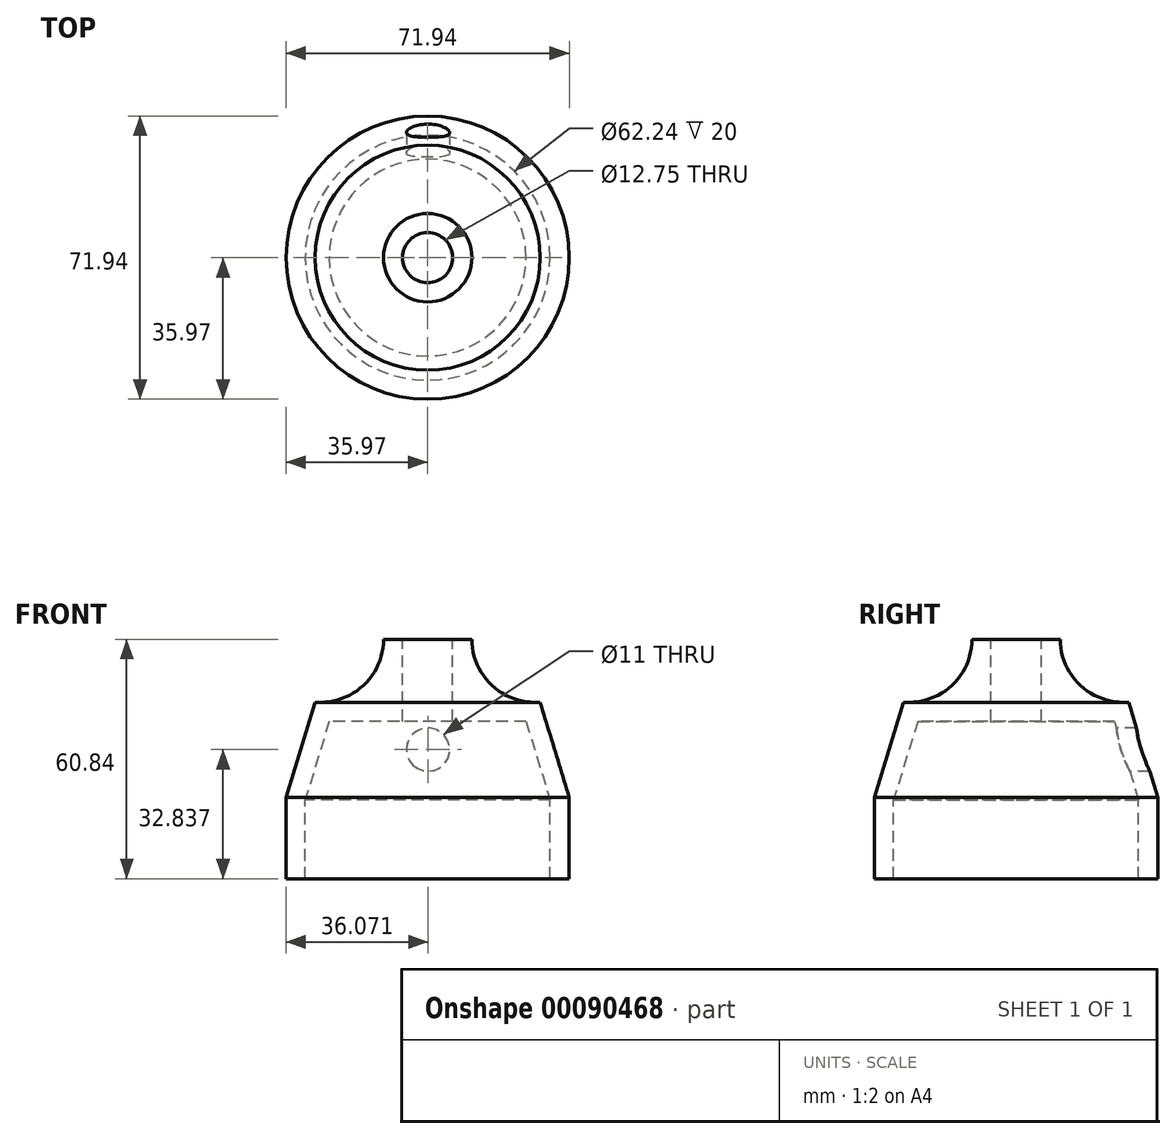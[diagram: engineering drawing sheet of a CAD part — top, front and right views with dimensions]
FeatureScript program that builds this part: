
annotation { "Feature Type Name" : "Feature", "Feature Type Description" : "" }
export const myFeature = defineFeature(function(context is Context, id is Id, definition is map)
    precondition{}
    {
        {
            var Q0;
            Q0=qCreatedBy(makeId("Front.planeOp"),FACE);
            var sketch = newSketch(context, id + "F0", { "sketchPlane" : qUnion([Q0])});
            skLineSegment(sketch, "E0.left", {"start": v(-31.12, -26.88) * mm, "end": v(-31.12, -6.88) * mm});
            skPoint(sketch, "E0.middle", {"position": v(0, -21.88) * mm});
            skLineSegment(sketch, "E1", {"start": v(-31.12, -6.88) * mm, "end": v(-25, 13.12) * mm});
            skLineSegment(sketch, "E2", {"start": v(0, 13.12) * mm, "end": v(0, -6.88) * mm});
            skPoint(sketch, "E3.middle", {"position": v(0, 13.12) * mm});
            skLineSegment(sketch, "E4", {"start": v(-25, 13.12) * mm, "end": v(-6.38, 13.12) * mm});
            skLineSegment(sketch, "E5.2", {"start": v(-35.97, -6.16) * mm, "end": v(-28.59, 17.96) * mm});
            skLineSegment(sketch, "E5.3", {"start": v(-35.97, -26.88) * mm, "end": v(-35.97, -6.16) * mm});
            skLineSegment(sketch, "E6", {"start": v(-35.97, -26.88) * mm, "end": v(-31.12, -26.88) * mm});
            skLineSegment(sketch, "E7", {"start": v(-28.59, 17.96) * mm, "end": v(-27.22, 17.96) * mm});
            skPoint(sketch, "E8.visualSharp", {"position": v(-11.22, 17.96) * mm});
            skArc(sketch, "E8.filletArc", {"start": v(-27.22, 17.96) * mm, "mid": v(-15.9, 22.65) * mm, "end": v(-11.22, 33.96) * mm});
            skLineSegment(sketch, "E9", {"start": v(-11.22, 33.96) * mm, "end": v(-6.38, 33.96) * mm});
            skLineSegment(sketch, "E10", {"start": v(-6.38, 33.96) * mm, "end": v(-6.38, 13.12) * mm});
            skSolve(sketch);
        }
        {
            var Q0;
            Q0=makeQuery(id+"F0.imprint","IMPRINT",FACE,{"disambiguationData":[TD([[makeQuery(id+"F0.imprint","IMPRINT",EDGE,{"derivedFrom":sQuery(id+"F0.wireOp",EDGE,"E0.left")}),1.0]])]});
            var Q1;
            Q1=sQuery(id+"F0.wireOp",EDGE,"E2");
            revolve(context, id + "F1", {"entities" : qUnion([Q0]), "axis" : qUnion([Q1]), "revolveType" : RevolveType.FULL});
        }
        {
            var Q0;
            Q0=qCreatedBy(makeId("Front.planeOp"),FACE);
            var sketch = newSketch(context, id + "F2", { "sketchPlane" : qUnion([Q0])});
            skLineSegment(sketch, "E11", {"start": v(-32.5, 5.96) * mm, "end": v(32.71, 5.96) * mm});
            skCircle(sketch, "E12", {"center": v(0.1, 5.96) * mm, "radius": 5.5 * mm});
            skSolve(sketch);
        }
        {
            var Q0;
            Q0 = qSketchRegion(id + "F2", true);
            extrude(context, id + "F3", {"entities" : qUnion([Q0]), "operationType" : NewBodyOperationType.REMOVE, "endBound" : BoundingType.THROUGH_ALL, "oppositeDirection" : true, "depth" : 25 * mm});
        }
        {
            var Q0;
            Q0=qCreatedBy(makeId("Front.planeOp"),FACE);
            var sketch = newSketch(context, id + "F4", { "sketchPlane" : qUnion([Q0])});
            skLineSegment(sketch, "E13", {"start": v(0, 0) * mm, "end": v(0, 45.74) * mm});
            skSolve(sketch);
        }
        {
            var Q0;
            Q0=makeQuery(id+"F1.opRevolve","SWEPT_BODY",BODY,{"disambiguationData":[OSD([sQuery(id+"F0.wireOp",EDGE,"E0.left"),sQuery(id+"F0.wireOp",EDGE,"E1"),sQuery(id+"F0.wireOp",EDGE,"E4"),sQuery(id+"F0.wireOp",EDGE,"E5.2"),sQuery(id+"F0.wireOp",EDGE,"E5.3"),sQuery(id+"F0.wireOp",EDGE,"E6"),sQuery(id+"F0.wireOp",EDGE,"E7"),sQuery(id+"F0.wireOp",EDGE,"E8.filletArc"),sQuery(id+"F0.wireOp",EDGE,"E9"),sQuery(id+"F0.wireOp",EDGE,"E10")])]});
            var Q1;
            Q1=sQuery(id+"F4.wireOp",EDGE,"E13");
            circularPattern(context, id + "F5", {"entities" : qUnion([Q0]), "axis" : qUnion([Q1]), "angle" : 120 * degree, "instanceCount" : 3});
        }
        {
            var Q0;
            Q0=makeQuery(id+"F5.opPattern","COPY",BODY,{"derivedFrom":makeQuery(id+"F1.opRevolve","SWEPT_BODY",BODY,{"disambiguationData":[OSD([sQuery(id+"F0.wireOp",EDGE,"E0.left"),sQuery(id+"F0.wireOp",EDGE,"E1"),sQuery(id+"F0.wireOp",EDGE,"E4"),sQuery(id+"F0.wireOp",EDGE,"E5.2"),sQuery(id+"F0.wireOp",EDGE,"E5.3"),sQuery(id+"F0.wireOp",EDGE,"E6"),sQuery(id+"F0.wireOp",EDGE,"E7"),sQuery(id+"F0.wireOp",EDGE,"E8.filletArc"),sQuery(id+"F0.wireOp",EDGE,"E9"),sQuery(id+"F0.wireOp",EDGE,"E10")])]}),"instanceName":"1"});
            deleteBodies(context, id + "F6", {"entities" : qUnion([Q0])});
        }
        {
            var Q0;
            Q0=makeQuery(id+"F5.opPattern","COPY",BODY,{"derivedFrom":makeQuery(id+"F1.opRevolve","SWEPT_BODY",BODY,{"disambiguationData":[OSD([sQuery(id+"F0.wireOp",EDGE,"E0.left"),sQuery(id+"F0.wireOp",EDGE,"E1"),sQuery(id+"F0.wireOp",EDGE,"E4"),sQuery(id+"F0.wireOp",EDGE,"E5.2"),sQuery(id+"F0.wireOp",EDGE,"E5.3"),sQuery(id+"F0.wireOp",EDGE,"E6"),sQuery(id+"F0.wireOp",EDGE,"E7"),sQuery(id+"F0.wireOp",EDGE,"E8.filletArc"),sQuery(id+"F0.wireOp",EDGE,"E9"),sQuery(id+"F0.wireOp",EDGE,"E10")])]}),"instanceName":"2"});
            deleteBodies(context, id + "F7", {"entities" : qUnion([Q0])});
        }
        {
            var Q0;
            Q0=qCreatedBy(makeId("Front.planeOp"),FACE);
            var sketch = newSketch(context, id + "F8", { "sketchPlane" : qUnion([Q0])});
            skLineSegment(sketch, "E14", {"start": v(0, 0) * mm, "end": v(0, 47.33) * mm});
            skSolve(sketch);
        }
        {
            var Q0;
            Q0=makeQuery(id+"F1.opRevolve","SWEPT_BODY",BODY,{"disambiguationData":[OSD([sQuery(id+"F0.wireOp",EDGE,"E0.left"),sQuery(id+"F0.wireOp",EDGE,"E1"),sQuery(id+"F0.wireOp",EDGE,"E4"),sQuery(id+"F0.wireOp",EDGE,"E5.2"),sQuery(id+"F0.wireOp",EDGE,"E5.3"),sQuery(id+"F0.wireOp",EDGE,"E6"),sQuery(id+"F0.wireOp",EDGE,"E7"),sQuery(id+"F0.wireOp",EDGE,"E8.filletArc"),sQuery(id+"F0.wireOp",EDGE,"E9"),sQuery(id+"F0.wireOp",EDGE,"E10")])]});
            var Q1;
            Q1=sQuery(id+"F8.wireOp",EDGE,"E14");
            circularPattern(context, id + "F9", {"entities" : qUnion([Q0]), "axis" : qUnion([Q1]), "angle" : 120 * degree, "instanceCount" : 3});
        }
        {
            var Q0;
            Q0=makeQuery(id+"F9.opPattern","COPY",BODY,{"derivedFrom":makeQuery(id+"F1.opRevolve","SWEPT_BODY",BODY,{"disambiguationData":[OSD([sQuery(id+"F0.wireOp",EDGE,"E0.left"),sQuery(id+"F0.wireOp",EDGE,"E1"),sQuery(id+"F0.wireOp",EDGE,"E4"),sQuery(id+"F0.wireOp",EDGE,"E5.2"),sQuery(id+"F0.wireOp",EDGE,"E5.3"),sQuery(id+"F0.wireOp",EDGE,"E6"),sQuery(id+"F0.wireOp",EDGE,"E7"),sQuery(id+"F0.wireOp",EDGE,"E8.filletArc"),sQuery(id+"F0.wireOp",EDGE,"E9"),sQuery(id+"F0.wireOp",EDGE,"E10")])]}),"instanceName":"2"});
            deleteBodies(context, id + "F10", {"entities" : qUnion([Q0])});
        }
        {
            var Q0;
            Q0=makeQuery(id+"F9.opPattern","COPY",BODY,{"derivedFrom":makeQuery(id+"F1.opRevolve","SWEPT_BODY",BODY,{"disambiguationData":[OSD([sQuery(id+"F0.wireOp",EDGE,"E0.left"),sQuery(id+"F0.wireOp",EDGE,"E1"),sQuery(id+"F0.wireOp",EDGE,"E4"),sQuery(id+"F0.wireOp",EDGE,"E5.2"),sQuery(id+"F0.wireOp",EDGE,"E5.3"),sQuery(id+"F0.wireOp",EDGE,"E6"),sQuery(id+"F0.wireOp",EDGE,"E7"),sQuery(id+"F0.wireOp",EDGE,"E8.filletArc"),sQuery(id+"F0.wireOp",EDGE,"E9"),sQuery(id+"F0.wireOp",EDGE,"E10")])]}),"instanceName":"1"});
            deleteBodies(context, id + "F11", {"entities" : qUnion([Q0])});
        }
    });
